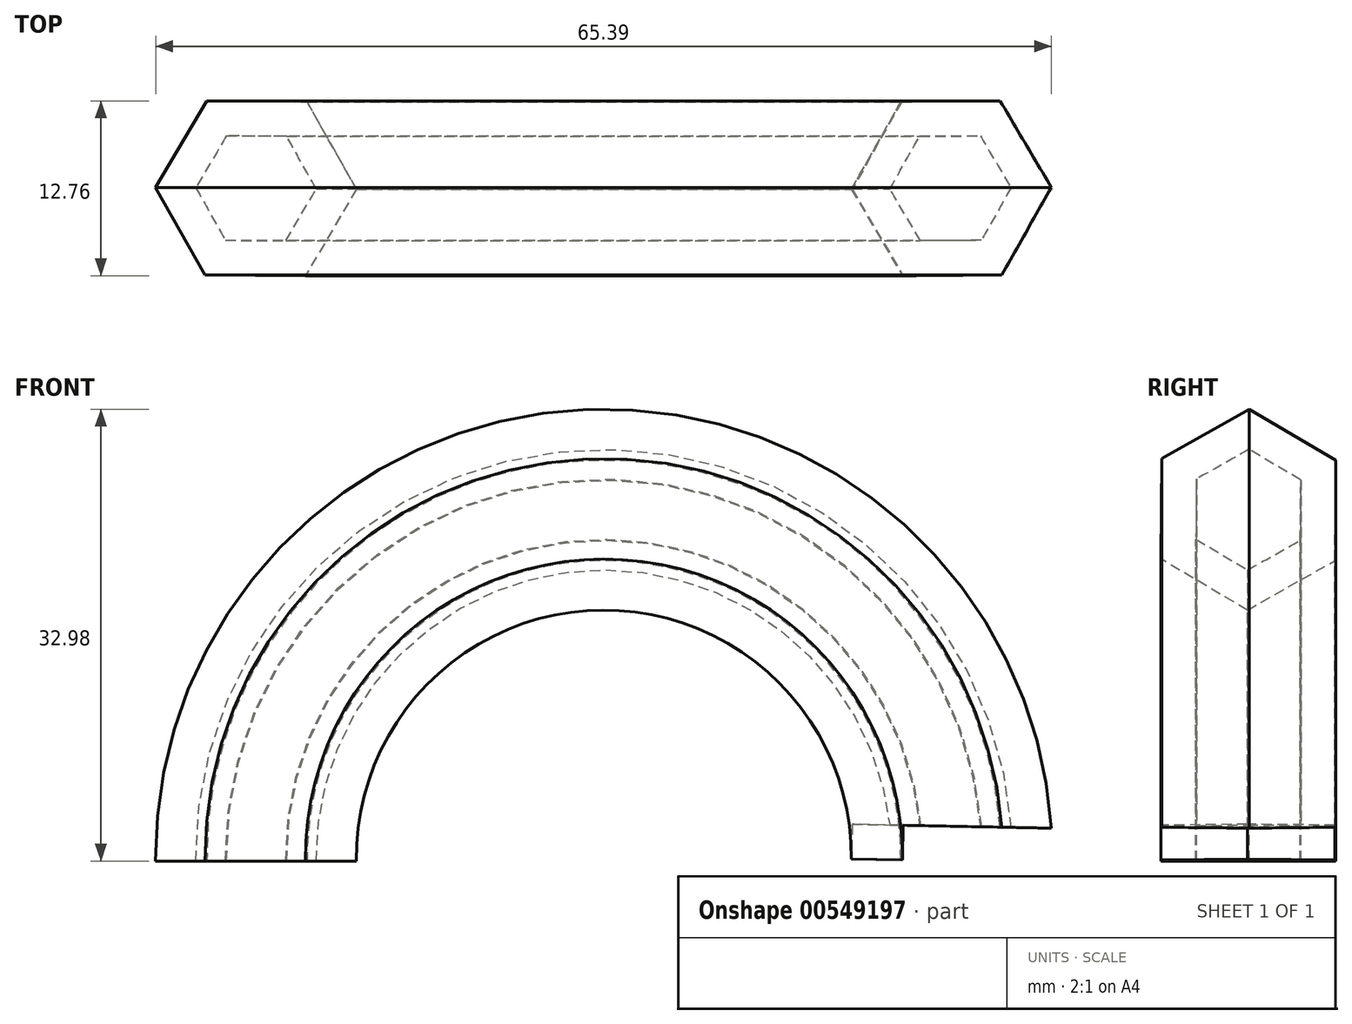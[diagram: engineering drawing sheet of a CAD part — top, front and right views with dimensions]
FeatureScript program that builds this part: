
annotation { "Feature Type Name" : "Feature", "Feature Type Description" : "" }
export const myFeature = defineFeature(function(context is Context, id is Id, definition is map)
    precondition{}
    {
        {
            var Q0;
            Q0=qCreatedBy(makeId("Front.planeOp"),FACE);
            var sketch = newSketch(context, id + "F0", { "sketchPlane" : qUnion([Q0])});
            skArc(sketch, "E0", {"start": v(50.8, 0) * mm, "mid": v(25.4, 25.65) * mm, "end": v(0, 0) * mm});
            skSolve(sketch);
        }
        {
            var Q0;
            Q0=qCreatedBy(makeId("Top.planeOp"),FACE);
            var sketch = newSketch(context, id + "F1", { "sketchPlane" : qUnion([Q0])});
            skCircle(sketch, "E1.cCircle", {"center": v(0, 0) * mm, "radius": 6.35 * mm, "construction": true});
            skLineSegment(sketch, "E1.0", {"start": v(7.33, -0.07) * mm, "end": v(3.6, -6.38) * mm});
            skLineSegment(sketch, "E1.1", {"start": v(3.6, -6.38) * mm, "end": v(-3.72, -6.32) * mm});
            skLineSegment(sketch, "E1.2", {"start": v(-3.72, -6.32) * mm, "end": v(-7.33, 0.07) * mm});
            skLineSegment(sketch, "E1.3", {"start": v(-7.33, 0.07) * mm, "end": v(-3.6, 6.38) * mm});
            skLineSegment(sketch, "E1.4", {"start": v(-3.6, 6.38) * mm, "end": v(3.72, 6.32) * mm});
            skLineSegment(sketch, "E1.5", {"start": v(3.72, 6.32) * mm, "end": v(7.33, -0.07) * mm});
            skPoint(sketch, "E1.0.midPoint", {"position": v(5.47, -3.22) * mm});
            skSolve(sketch);
        }
        {
            var Q0;
            Q0=makeQuery(id+"F1.imprint","IMPRINT",FACE,{"disambiguationData":[TD([[makeQuery(id+"F1.imprint","IMPRINT",EDGE,{"derivedFrom":sQuery(id+"F1.wireOp",EDGE,"E1.0")}),-1.0]])]});
            var Q1;
            Q1=sQuery(id+"F0.wireOp",EDGE,"E0");
            sweep(context, id + "F2", {"profiles" : qUnion([Q0]), "path" : qUnion([Q1])});
        }
        {
            var Q0;
            Q0=makeQuery(id+"F2.opSweep","CAP_FACE",FACE,{"disambiguationData":[OSD([sQuery(id+"F0.wireOp",VERTEX,"E0.end"),sQuery(id+"F1.wireOp",EDGE,"E1.0"),sQuery(id+"F1.wireOp",EDGE,"E1.1"),sQuery(id+"F1.wireOp",EDGE,"E1.2"),sQuery(id+"F1.wireOp",EDGE,"E1.3"),sQuery(id+"F1.wireOp",EDGE,"E1.4"),sQuery(id+"F1.wireOp",EDGE,"E1.5")])],"isStart":true});
            shell(context, id + "F3", {"entities" : qUnion([Q0]), "thickness" : 2.54 * mm});
        }
        {
            var Q0;
            Q0=makeQuery(id+"F2.opSweep","CAP_FACE",FACE,{"disambiguationData":[OSD([sQuery(id+"F0.wireOp",VERTEX,"E0.start"),sQuery(id+"F1.wireOp",EDGE,"E1.0"),sQuery(id+"F1.wireOp",EDGE,"E1.1"),sQuery(id+"F1.wireOp",EDGE,"E1.2"),sQuery(id+"F1.wireOp",EDGE,"E1.3"),sQuery(id+"F1.wireOp",EDGE,"E1.4"),sQuery(id+"F1.wireOp",EDGE,"E1.5")])],"isStart":false});
            extrude(context, id + "F4", {"entities" : qUnion([Q0]), "operationType" : NewBodyOperationType.REMOVE, "oppositeDirection" : true, "depth" : 2.54 * mm, "offsetDistance" : 25.4 * mm});
        }
    });
